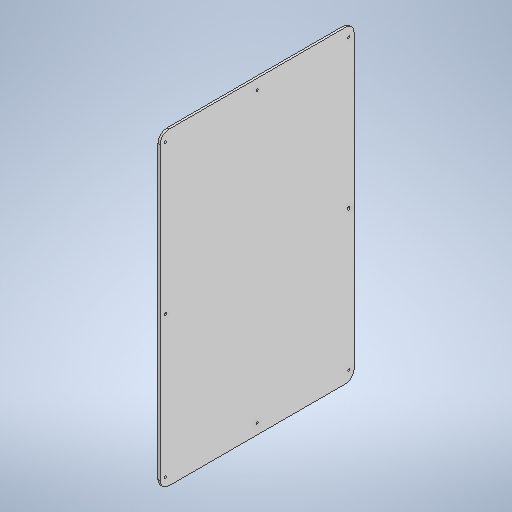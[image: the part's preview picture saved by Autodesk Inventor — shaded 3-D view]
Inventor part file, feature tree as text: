
AUTODESK INVENTOR PART (.ipt)
format: ipt  version: 2025 (Build 290162010, 162A)  size: 260,096 bytes
history: native  units: in
note: dims shown in document units (in); Inventor stores cm internally (conversion verified against a paired STEP export)
features: extrude x1, fillet x1, sketch x1
ambient origin geometry x8: Origin, YZ Plane, XZ Plane, XY Plane, X Axis, Y Axis, Z Axis, Center Point
bodies: Solid1 (feature_tree)
feature tree (3):
  extrude  "Extrusion1"  Depth=10.7874in
  fillet  "Fillet1"  Radius=0.1181in
  sketch  "Sketch1"  dims[d0=17.1654in d1=10.7874in d3=0.1181in d4=0.1181in d5=0.1181in d6=10.1969in d7=5.0984in d8=0.0in d9=0.1181in d10=8.2579in d11=0.05in d12=0.1181in d13=0.1181in d14=0.0591in d15=0.122in d16=0.0in d17=0.5in]
